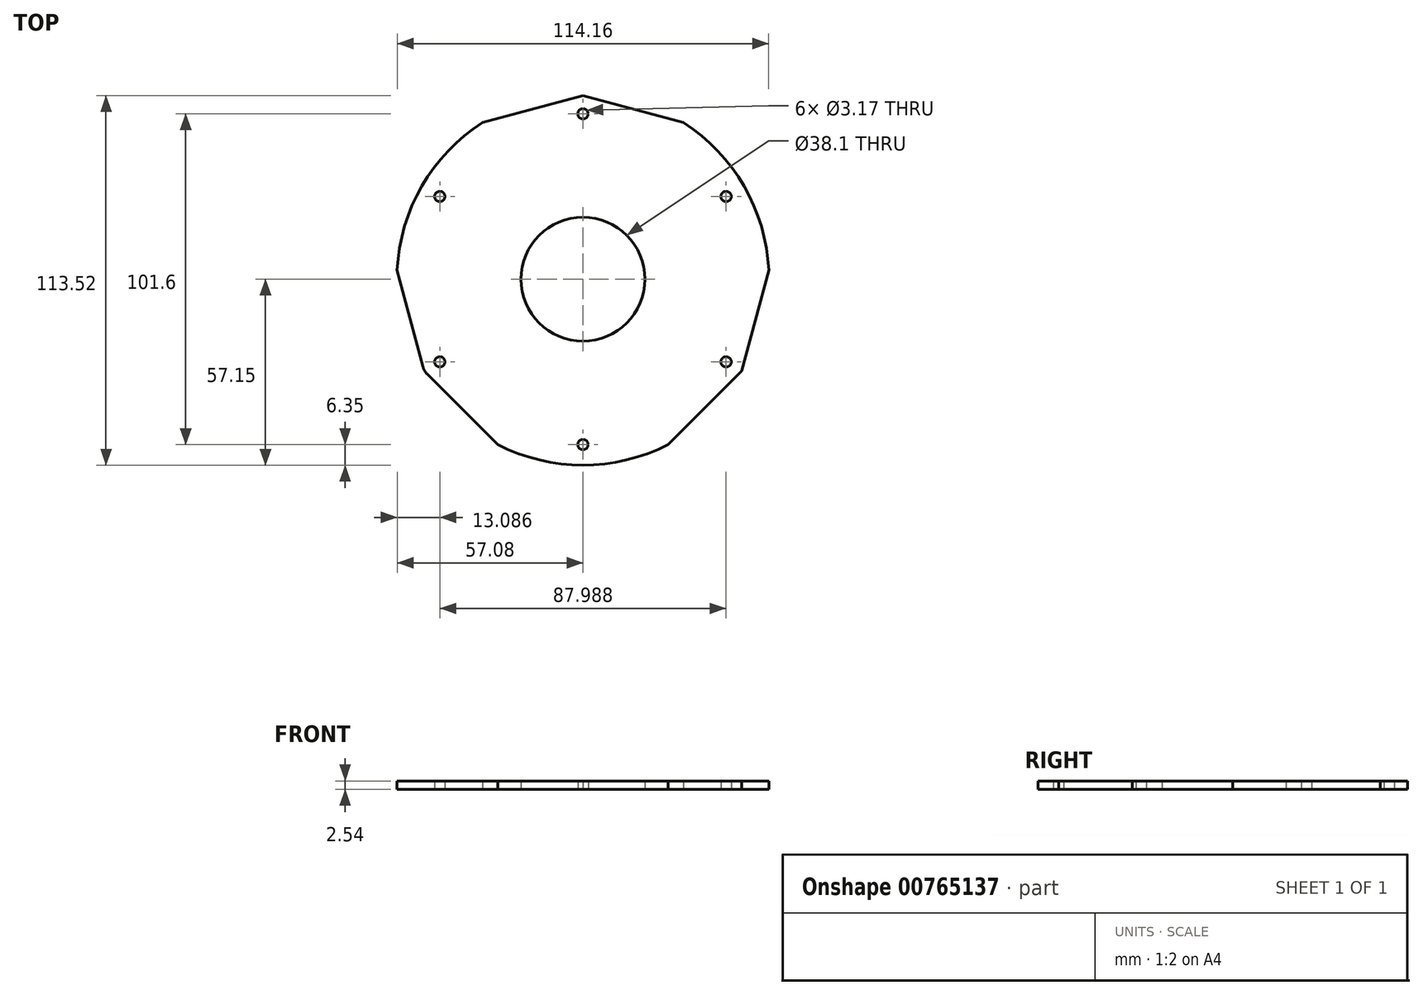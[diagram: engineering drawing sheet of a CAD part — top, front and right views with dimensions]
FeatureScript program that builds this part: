
annotation { "Feature Type Name" : "Feature", "Feature Type Description" : "" }
export const myFeature = defineFeature(function(context is Context, id is Id, definition is map)
    precondition{}
    {
        {
            var Q0;
            Q0=qCreatedBy(makeId("Top.planeOp"),FACE);
            var sketch = newSketch(context, id + "F0", { "sketchPlane" : qUnion([Q0])});
            skCircle(sketch, "E0.cCircle", {"center": v(0, 0) * mm, "radius": 101.6 * mm, "construction": true});
            skLineSegment(sketch, "E1", {"start": v(0, 0) * mm, "end": v(0, 101.6) * mm});
            skCircle(sketch, "E2", {"center": v(0, 0) * mm, "radius": 47.63 * mm});
            skPoint(sketch, "E3", {"position": v(-44, -25.4) * mm});
            skPoint(sketch, "E4", {"position": v(44, -25.4) * mm});
            skPoint(sketch, "E5", {"position": v(0, 50.8) * mm});
            skArc(sketch, "E6", {"start": v(-30.9, 48.07) * mm, "mid": v(-49.5, 28.57) * mm, "end": v(-57.08, 2.73) * mm});
            skArc(sketch, "E7", {"start": v(57.08, 2.73) * mm, "mid": v(49.5, 28.58) * mm, "end": v(30.9, 48.07) * mm});
            skArc(sketch, "E8", {"start": v(-26.18, -50.8) * mm, "mid": v(0, -57.15) * mm, "end": v(26.18, -50.8) * mm});
            skCircle(sketch, "E9", {"center": v(-44, -25.4) * mm, "radius": 1.59 * mm});
            skCircle(sketch, "E10", {"center": v(44, -25.4) * mm, "radius": 1.59 * mm});
            skCircle(sketch, "E11", {"center": v(0, 50.8) * mm, "radius": 1.59 * mm});
            skPoint(sketch, "E12", {"position": v(-44, 25.4) * mm});
            skPoint(sketch, "E13", {"position": v(0, -50.8) * mm});
            skPoint(sketch, "E14", {"position": v(44, 25.4) * mm});
            skCircle(sketch, "E15", {"center": v(-44, 25.4) * mm, "radius": 1.59 * mm});
            skCircle(sketch, "E16", {"center": v(44, 25.4) * mm, "radius": 1.59 * mm});
            skCircle(sketch, "E17", {"center": v(0, -50.8) * mm, "radius": 1.59 * mm});
            skLineSegment(sketch, "E18", {"start": v(-30.9, 48.07) * mm, "end": v(0, 56.37) * mm});
            skLineSegment(sketch, "E19", {"start": v(0, 56.37) * mm, "end": v(30.9, 48.07) * mm});
            skLineSegment(sketch, "E20.1.0", {"start": v(-26.18, -50.8) * mm, "end": v(-48.82, -28.19) * mm});
            skLineSegment(sketch, "E20.1.1", {"start": v(-48.82, -28.19) * mm, "end": v(-57.08, 2.73) * mm});
            skLineSegment(sketch, "E20.2.0", {"start": v(57.08, 2.73) * mm, "end": v(48.82, -28.19) * mm});
            skLineSegment(sketch, "E20.2.1", {"start": v(48.82, -28.19) * mm, "end": v(26.18, -50.8) * mm});
            skCircle(sketch, "E21", {"center": v(0, 0) * mm, "radius": 19.05 * mm});
            skSolve(sketch);
        }
        {
            var Q0;
            Q0=makeQuery(id+"F0.imprint","IMPRINT",FACE,{"disambiguationData":[TD([[makeQuery(id+"F0.imprint","IMPRINT",EDGE,{"derivedFrom":sQuery(id+"F0.wireOp",EDGE,"E2")}),-1.0]])]});
            var Q1;
            Q1=makeQuery(id+"F0.imprint","IMPRINT",FACE,{"disambiguationData":[TD([[makeQuery(id+"F0.imprint","IMPRINT",EDGE,{"derivedFrom":sQuery(id+"F0.wireOp",EDGE,"E2")}),1.0]])]});
            extrude(context, id + "F1", {"entities" : qUnion([Q0, Q1]), "depth" : 2.54 * mm, "offsetDistance" : 25.4 * mm});
        }
        {
            var Q0;
            Q0=makeQuery(id+"F1.opExtrude","SWEPT_EDGE",EDGE,{"disambiguationData":[OSD([sQuery(id+"F0.wireOp",EDGE,"E20.1.0"),sQuery(id+"F0.wireOp",EDGE,"E20.1.1")])]});
            fillet(context, id + "F2", {"entities" : qUnion([Q0]), "radius" : 5.08 * mm, "tangentPropagation" : true, "allowEdgeOverflow" : false});
        }
    });
